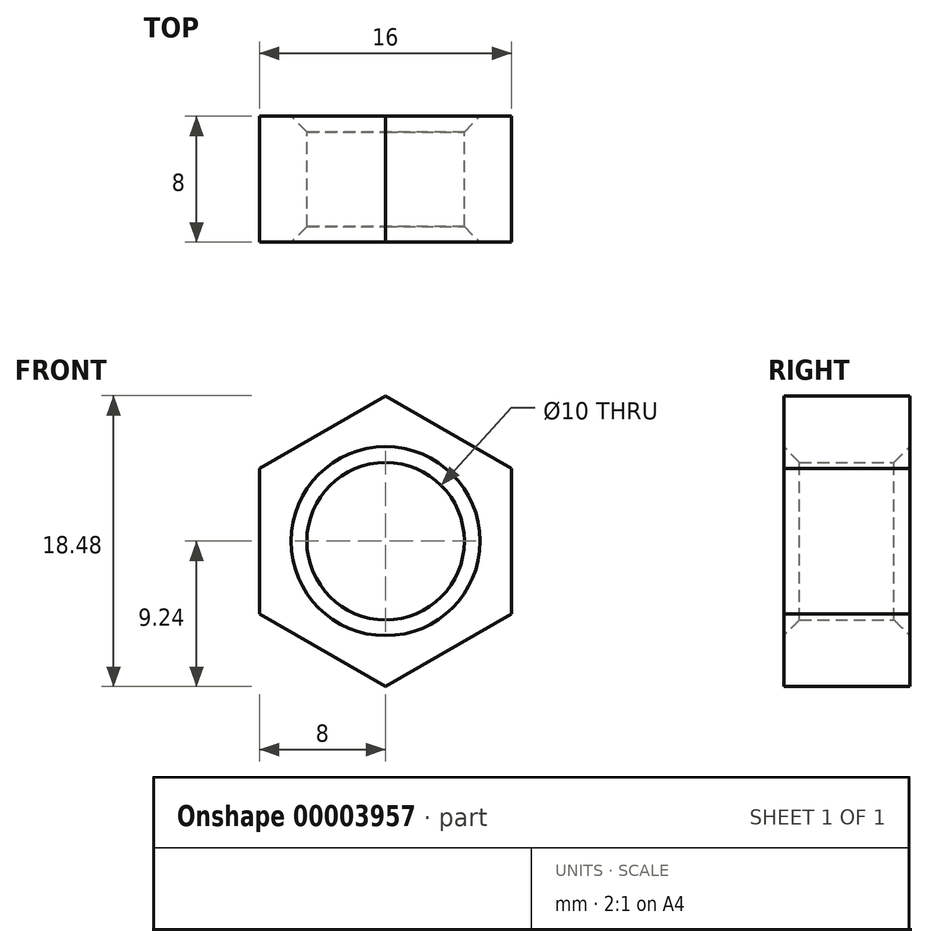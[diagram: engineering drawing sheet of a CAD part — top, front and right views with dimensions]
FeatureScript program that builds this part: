
annotation { "Feature Type Name" : "Feature", "Feature Type Description" : "" }
export const myFeature = defineFeature(function(context is Context, id is Id, definition is map)
    precondition{}
    {
        {
            var Q0;
            Q0=qCreatedBy(makeId("Front.planeOp"),FACE);
            var sketch = newSketch(context, id + "F0", { "sketchPlane" : qUnion([Q0])});
            skCircle(sketch, "E0", {"center": v(0, 0) * mm, "radius": 5 * mm});
            skLineSegment(sketch, "E1", {"start": v(8, 0) * mm, "end": v(8, 4.62) * mm});
            skLineSegment(sketch, "E2", {"start": v(8, 4.62) * mm, "end": v(0, 9.24) * mm});
            skLineSegment(sketch, "E3.0.MirrorCS", {"start": v(8, 0) * mm, "end": v(8, -4.62) * mm});
            skLineSegment(sketch, "E4.0.MirrorCS", {"start": v(8, -4.62) * mm, "end": v(0, -9.24) * mm});
            skLineSegment(sketch, "E5.0.MirrorCS", {"start": v(-8, 4.62) * mm, "end": v(0, 9.24) * mm});
            skLineSegment(sketch, "E6.0.MirrorCS", {"start": v(-8, 0) * mm, "end": v(-8, 4.62) * mm});
            skLineSegment(sketch, "E7.0.MirrorCS", {"start": v(-8, 0) * mm, "end": v(-8, -4.62) * mm});
            skLineSegment(sketch, "E8.0.MirrorCS", {"start": v(-8, -4.62) * mm, "end": v(0, -9.24) * mm});
            skSolve(sketch);
        }
        {
            var Q0;
            Q0 = qSketchRegion(id + "F0", true);
            extrude(context, id + "F1", {"entities" : qUnion([Q0]), "depth" : 8 * mm});
        }
        {
            var Q0;
            Q0=makeQuery(id+"F1.opExtrude","CAP_EDGE",EDGE,{"disambiguationData":[OSD([sQuery(id+"F0.wireOp",EDGE,"E0")])],"isStart":true});
            var Q1;
            Q1=makeQuery(id+"F1.opExtrude","CAP_EDGE",EDGE,{"disambiguationData":[OSD([sQuery(id+"F0.wireOp",EDGE,"E0")])],"isStart":false});
            chamfer(context, id + "F2", {"entities" : qUnion([Q0, Q1]), "width" : 1 * mm, "tangentPropagation" : true});
        }
    });
